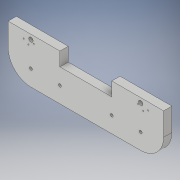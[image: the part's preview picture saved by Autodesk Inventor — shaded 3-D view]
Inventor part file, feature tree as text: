
AUTODESK INVENTOR PART (.ipt)
format: ipt  version: 2019 (Build 230136000, 136)  size: 167,424 bytes
history: native  units: in
note: dims shown in document units (in); Inventor stores cm internally (conversion verified against a paired STEP export)
features: sketch x5, hole x3, extrude x2
ambient origin geometry x8: Origin, YZ Plane, XZ Plane, XY Plane, X Axis, Y Axis, Z Axis, Center Point
bodies: Solid1 (feature_tree)
feature tree (10):
  extrude  "Extrusion1"  Depth=3.5in
  hole  "Hole1"  [1 undecoded]
  extrude  "Extrusion2"  Depth=3.5in
  hole  "Hole2"  [1 undecoded]
  hole  "Hole3"  [1 undecoded]
  sketch  "Sketch1"  dims[d0=17.0in d1=3.5in]
  sketch  "Sketch2"  dims[d2=2.5in d3=2.5in]
  sketch  "Sketch3"  dims[d4=0.9055in d5=0.0in d6=3.5in]
  sketch  "Sketch4"  dims[d7=1.75in d8=1.75in]
  sketch  "Sketch5"  dims[d9=1.75in d10=1.75in d11=17.0in d12=2.5in d13=5.6667in d14=5.6667in d15=2.5in d16=0.311in d17=0.75in d18=0.375in d19=0.25in d20=0.5635in d21=1.0in d22=0.8108in d27=17.0in d28=5.6667in d29=5.6667in d30=1.5in d31=0.0in d32=1.5in d33=1.5in d34=0.5in d35=0.5in d38=0.0in d39=0.0in d40=0.472in d41=0.75in d42=0.375in d43=0.25in d44=0.5635in d45=1.0in d46=0.8108in d47=0.305in d48=0.253in d49=0.276in d50=0.61in d51=0.804in d52=0.305in d53=0.305in d54=0.253in d55=0.61in d56=0.276in d57=0.305in d58=0.804in d59=0.125in d60=0.75in d61=0.375in d62=0.25in d63=0.5635in d64=1.0in d65=0.8108in]
note: 3 required parameter values undecoded (feature->parameter linkage not recoverable at this tier; creation-order binding heuristic only, values carry confidence <= 0.55)
